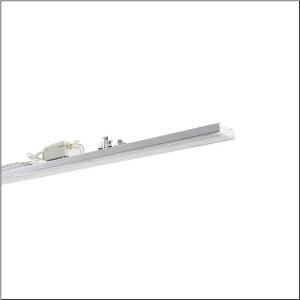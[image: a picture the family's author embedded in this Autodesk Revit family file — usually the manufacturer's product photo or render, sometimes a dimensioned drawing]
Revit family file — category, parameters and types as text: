
# Revit family: licross_r__21_recessed_ho_52tl1edn4axs_2080
name_source: partatom
category: Lighting Fixtures
units: mm (PartAtom-declared; Revit-internal decimal feet)

## family parameters
Cut with Voids When Loaded = No
Host = Face
Light Source = No
Part Type = Normal
Room Calculation Point = No
Round Connector Dimension = Use Diameter
Shared = No

## types (1)
- --- (1 x LED, 10000 lm, 56.1 W, 4000K)
    Apparent Load = 56 VA
    CIE Flux Codes = 85 95 99 100 100
    Color Rendering = 80
    Color Temperature = 4000K
    Default Elevation = 1800 mm
    Description = Licross® 21 Recessed HO, luminaire insert, of sheet steel, galvanised, coil coated, white, length: 1.500mm, width: 66mm, height: 67mm, LED rated luminous flux: 10.000lm, light colour: 840, control gear: DALI 2, with plug, 5-pole, with phase selection, mains connection: 220..240V, AC, 50/60Hz, rated input power: 56W, halogen-free wiring, primary light control with lens, of plastic, primary optical cover: cover, of PMMA, light emission: direct distribution, primary light characteristic: symmetric, protection rating (complete): IP40, insulation class (complete): insulation class I (protective earthing), certification: CE, ENEC, VDE, UKCA, protection symbol: D if used in an environment without relevant dust loads with corresponding accessories, impact resistance: IK06, permissible ambient temperature for indoor applications: -25..+40°C, corresponds to IFS (International Featured Standards) requirements for safety and quality in the food industry, reducing of maximum allowable ambient temperature of 5°C with ceiling mounting, LABS conformity tested according to VDMA 24364:2018-05, packaging unit: 1 piece
    Height = 58 mm
    Lamp = 1 x LED
    Lamp Light Flux = 10000 lm
    Lamp Power = 56.1 W
    Lamp count = 1
    Length = 1500 mm
    Luminous efficacy = 178 lm/W
    Manufacturer = Siteco
    ModVariant = No
    Model = 52TL1EDN4AXS
    Mounting Place = Ceiling
    Mounting Type = Pendant
    Number of Poles = 1
    OnlyDefault = Yes
    Power Factor = 1
    Product Name = Licross® 21 Recessed HO
    Product group = luminaire insert
    ProductGroupID = 901
    Protection Class = Protection class I
    Protection Degree = IP 40
    RLX_Detail_Level = 1
    RLX_Emergency_Light_Flux = 0 lm
    RLX_Emergency_Type = 0
    RLX_Emergency_Type_DB = No
    RlxData = <blob elided: 24433 chars, md5=e48f734b>
    Socket = socket
    Standby Power = 0 W
    System Light Flux = 10000 lm
    System Power = 56 W
    Type Comments = factory setting: luminous flux: 100 % | dim-lin: 254 | 321 mA
    Type Image = l_1296930.jpg
    URL = http://relux.com
    VarID = @adj_056673
    Voltage = 0 V
    Weight = 0.00 kg
    Width = 66 mm

## geometry (parser evidence)
native form markers: Blend x4, Sweep x9
no freeform markers — native parametric forms only
